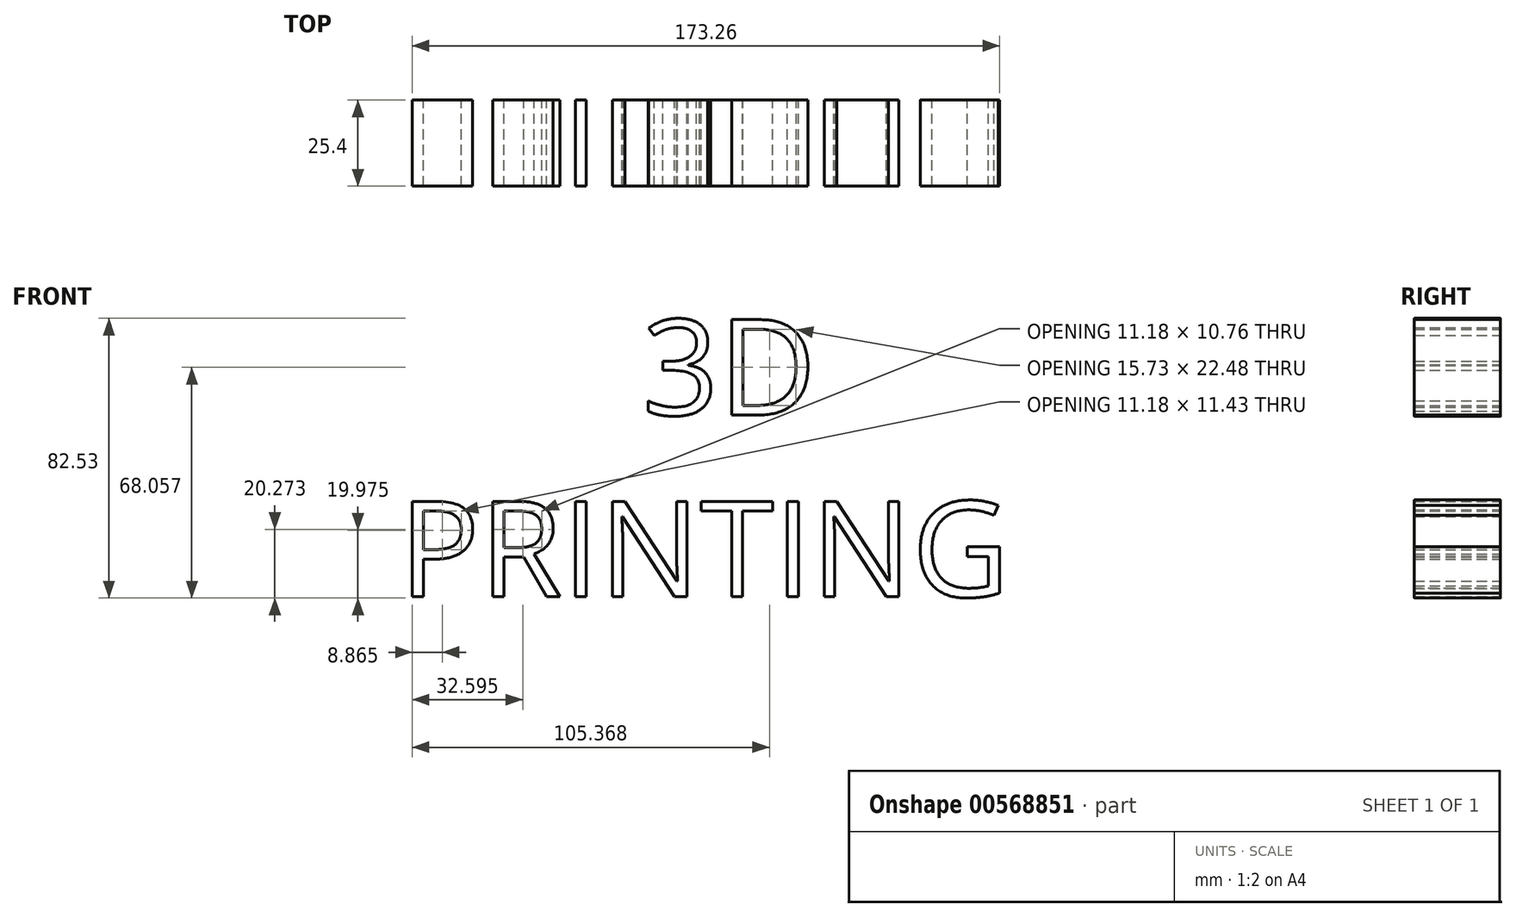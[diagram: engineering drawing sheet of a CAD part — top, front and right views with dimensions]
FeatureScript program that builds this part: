
annotation { "Feature Type Name" : "Feature", "Feature Type Description" : "" }
export const myFeature = defineFeature(function(context is Context, id is Id, definition is map)
    precondition{}
    {
        {
            var Q0;
            Q0=qCreatedBy(makeId("Front.planeOp"),FACE);
            var sketch = newSketch(context, id + "F0", { "sketchPlane" : qUnion([Q0])});
            skText(sketch, "E0", { "text": "         3D \n  PRINTING", "fontName": "OpenSans-Regular.ttf"});
            const initialGuessF0  = {"E0": [-0.04402, 0, 1, 0, 0.02838]};
            skSetInitialGuess(sketch, initialGuessF0);
            skSolve(sketch);
        }
        {
            var Q0;
            Q0 = qSketchRegion(id + "F0", true);
            extrude(context, id + "F1", {"entities" : qUnion([Q0]), "endBound" : BoundingType.SYMMETRIC, "depth" : 25.4 * mm, "offsetDistance" : 25.4 * mm});
        }
    });
